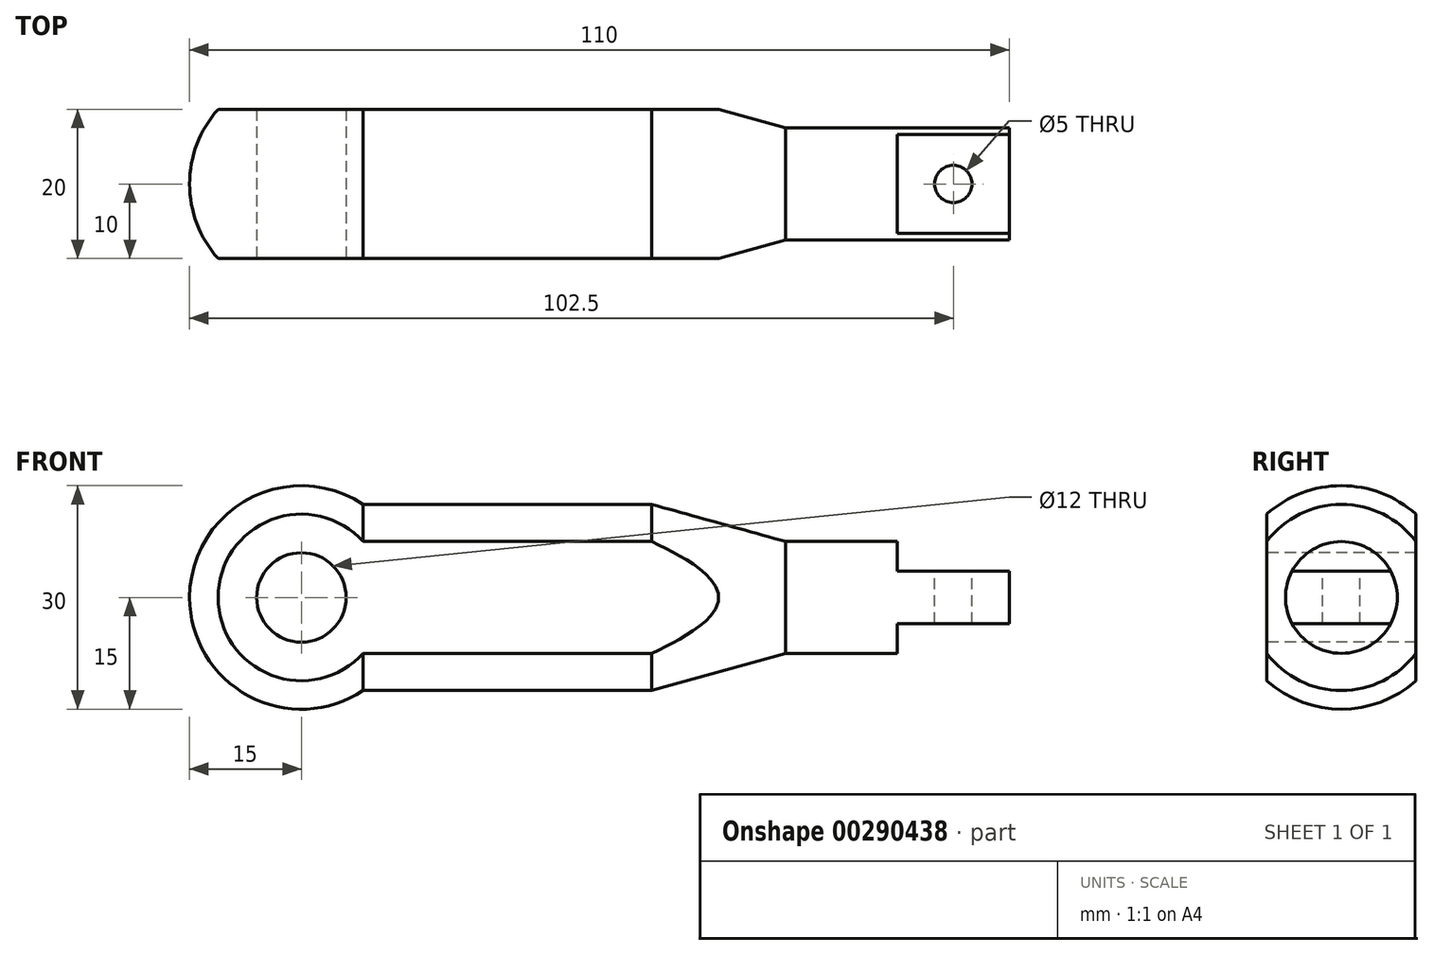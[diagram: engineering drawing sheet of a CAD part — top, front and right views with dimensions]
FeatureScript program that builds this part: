
annotation { "Feature Type Name" : "Feature", "Feature Type Description" : "" }
export const myFeature = defineFeature(function(context is Context, id is Id, definition is map)
    precondition{}
    {
        {
            var Q0;
            Q0=qCreatedBy(makeId("Front.planeOp"),FACE);
            var sketch = newSketch(context, id + "F0", { "sketchPlane" : qUnion([Q0])});
            skLineSegment(sketch, "E0", {"start": v(0, 0) * mm, "end": v(110.06, 0) * mm, "construction": true});
            skArc(sketch, "E1", {"start": v(-15, 0) * mm, "mid": v(-7.1, 13.22) * mm, "end": v(8.3, 12.5) * mm});
            skLineSegment(sketch, "E2", {"start": v(8.3, 12.5) * mm, "end": v(47, 12.5) * mm, "construction": true});
            skLineSegment(sketch, "E3", {"start": v(47, 12.5) * mm, "end": v(65, 7.5) * mm});
            skLineSegment(sketch, "E4", {"start": v(65, 7.5) * mm, "end": v(95, 7.5) * mm, "construction": true});
            skLineSegment(sketch, "E5", {"start": v(95, 7.5) * mm, "end": v(95, 0) * mm, "construction": true});
            skLineSegment(sketch, "E6", {"start": v(-15, 0) * mm, "end": v(95, 0) * mm});
            skLineSegment(sketch, "E7", {"start": v(95, 7.5) * mm, "end": v(95, 0) * mm});
            skLineSegment(sketch, "E8", {"start": v(65, 7.5) * mm, "end": v(95, 7.5) * mm});
            skLineSegment(sketch, "E9", {"start": v(8.3, 12.5) * mm, "end": v(47, 12.5) * mm});
            skSolve(sketch);
        }
        {
            var Q0;
            Q0 = qSketchRegion(id + "F0", true);
            var Q1;
            Q1=sQuery(id+"F0.wireOp",EDGE,"E0");
            revolve(context, id + "F1", {"entities" : qUnion([Q0]), "axis" : qUnion([Q1]), "revolveType" : RevolveType.FULL});
        }
        {
            var Q0;
            Q0=qCreatedBy(makeId("Front.planeOp"),FACE);
            var sketch = newSketch(context, id + "F2", { "sketchPlane" : qUnion([Q0])});
            skLineSegment(sketch, "E10.top", {"start": v(95, 3.5) * mm, "end": v(80, 3.5) * mm});
            skLineSegment(sketch, "E10.right", {"start": v(80, 7.5) * mm, "end": v(80, 3.5) * mm});
            skLineSegment(sketch, "E11", {"start": v(80, 7.5) * mm, "end": v(95, 7.5) * mm});
            skLineSegment(sketch, "E12", {"start": v(95, 7.5) * mm, "end": v(95, 3.5) * mm});
            skLineSegment(sketch, "E13", {"start": v(74.68, 0) * mm, "end": v(100.26, 0) * mm, "construction": true});
            skLineSegment(sketch, "E14.MirrorCS", {"start": v(95, -3.5) * mm, "end": v(80, -3.5) * mm});
            skLineSegment(sketch, "E15.MirrorCS", {"start": v(80, -7.5) * mm, "end": v(95, -7.5) * mm});
            skLineSegment(sketch, "E16.MirrorCS", {"start": v(80, -7.5) * mm, "end": v(80, -3.5) * mm});
            skLineSegment(sketch, "E17.MirrorCS", {"start": v(95, -7.5) * mm, "end": v(95, -3.5) * mm});
            skSolve(sketch);
        }
        {
            var Q0;
            Q0 = qSketchRegion(id + "F2", true);
            extrude(context, id + "F3", {"entities" : qUnion([Q0]), "operationType" : NewBodyOperationType.REMOVE, "endBound" : BoundingType.THROUGH_ALL, "oppositeDirection" : true, "depth" : 25 * mm, "hasSecondDirection" : true, "secondDirectionBound" : SecondDirectionBoundingType.THROUGH_ALL, "secondDirectionOppositeDirection" : false, "secondDirectionDepth" : 25 * mm});
        }
        {
            var Q0;
            Q0=makeQuery(id+"F1.opRevolve","SWEPT_FACE",FACE,{"disambiguationData":[OSD([sQuery(id+"F0.wireOp",EDGE,"E7")])]});
            var sketch = newSketch(context, id + "F4", { "sketchPlane" : qUnion([Q0])});
            skLineSegment(sketch, "E18", {"start": v(-10, 11.18) * mm, "end": v(-10, -25.4) * mm});
            skArc(sketch, "E19", {"start": v(-10, 11.18) * mm, "mid": v(-15, 0) * mm, "end": v(-10, -11.18) * mm});
            skLineSegment(sketch, "E20", {"start": v(10, 11.18) * mm, "end": v(10, -25.73) * mm});
            skLineSegment(sketch, "E21", {"start": v(0, 0) * mm, "end": v(0, 29.36) * mm, "construction": true});
            skArc(sketch, "E22.trimOffspring", {"start": v(10, -11.18) * mm, "mid": v(15, 0) * mm, "end": v(10, 11.18) * mm});
            skSolve(sketch);
        }
        {
            var Q0;
            Q0 = qSketchRegion(id + "F4", true);
            extrude(context, id + "F5", {"entities" : qUnion([Q0]), "operationType" : NewBodyOperationType.REMOVE, "endBound" : BoundingType.THROUGH_ALL, "oppositeDirection" : true, "depth" : 25 * mm});
        }
        {
            var Q0;
            Q0=makeQuery(id+"F3.boolean.opBoolean","COPY",FACE,{"derivedFrom":makeQuery(id+"F3.opExtrude","SWEPT_FACE",FACE,{"disambiguationData":[OSD([sQuery(id+"F2.wireOp",EDGE,"E10.top")])]})});
            var sketch = newSketch(context, id + "F6", { "sketchPlane" : qUnion([Q0])});
            skCircle(sketch, "E23", {"center": v(87.5, 0) * mm, "radius": 2.5 * mm});
            skPoint(sketch, "E24.0.end.orphan", {"position": v(95, -6.63) * mm});
            skPoint(sketch, "E24.0.start.orphan", {"position": v(95, 6.63) * mm});
            skSolve(sketch);
        }
        {
            var Q0;
            Q0 = qSketchRegion(id + "F6", true);
            extrude(context, id + "F7", {"entities" : qUnion([Q0]), "operationType" : NewBodyOperationType.REMOVE, "endBound" : BoundingType.THROUGH_ALL, "oppositeDirection" : true, "depth" : 25 * mm});
        }
        {
            var Q0;
            Q0=makeQuery(id+"F5.boolean.opBoolean","COPY",FACE,{"derivedFrom":makeQuery(id+"F5.opExtrude","SWEPT_FACE",FACE,{"disambiguationData":[OSD([sQuery(id+"F4.wireOp",EDGE,"E18")])]})});
            var sketch = newSketch(context, id + "F8", { "sketchPlane" : qUnion([Q0])});
            skCircle(sketch, "E25", {"center": v(0, 0) * mm, "radius": 6 * mm});
            skSolve(sketch);
        }
        {
            var Q0;
            Q0 = qSketchRegion(id + "F8", true);
            extrude(context, id + "F9", {"entities" : qUnion([Q0]), "operationType" : NewBodyOperationType.REMOVE, "endBound" : BoundingType.THROUGH_ALL, "oppositeDirection" : true, "depth" : 25 * mm});
        }
    });
